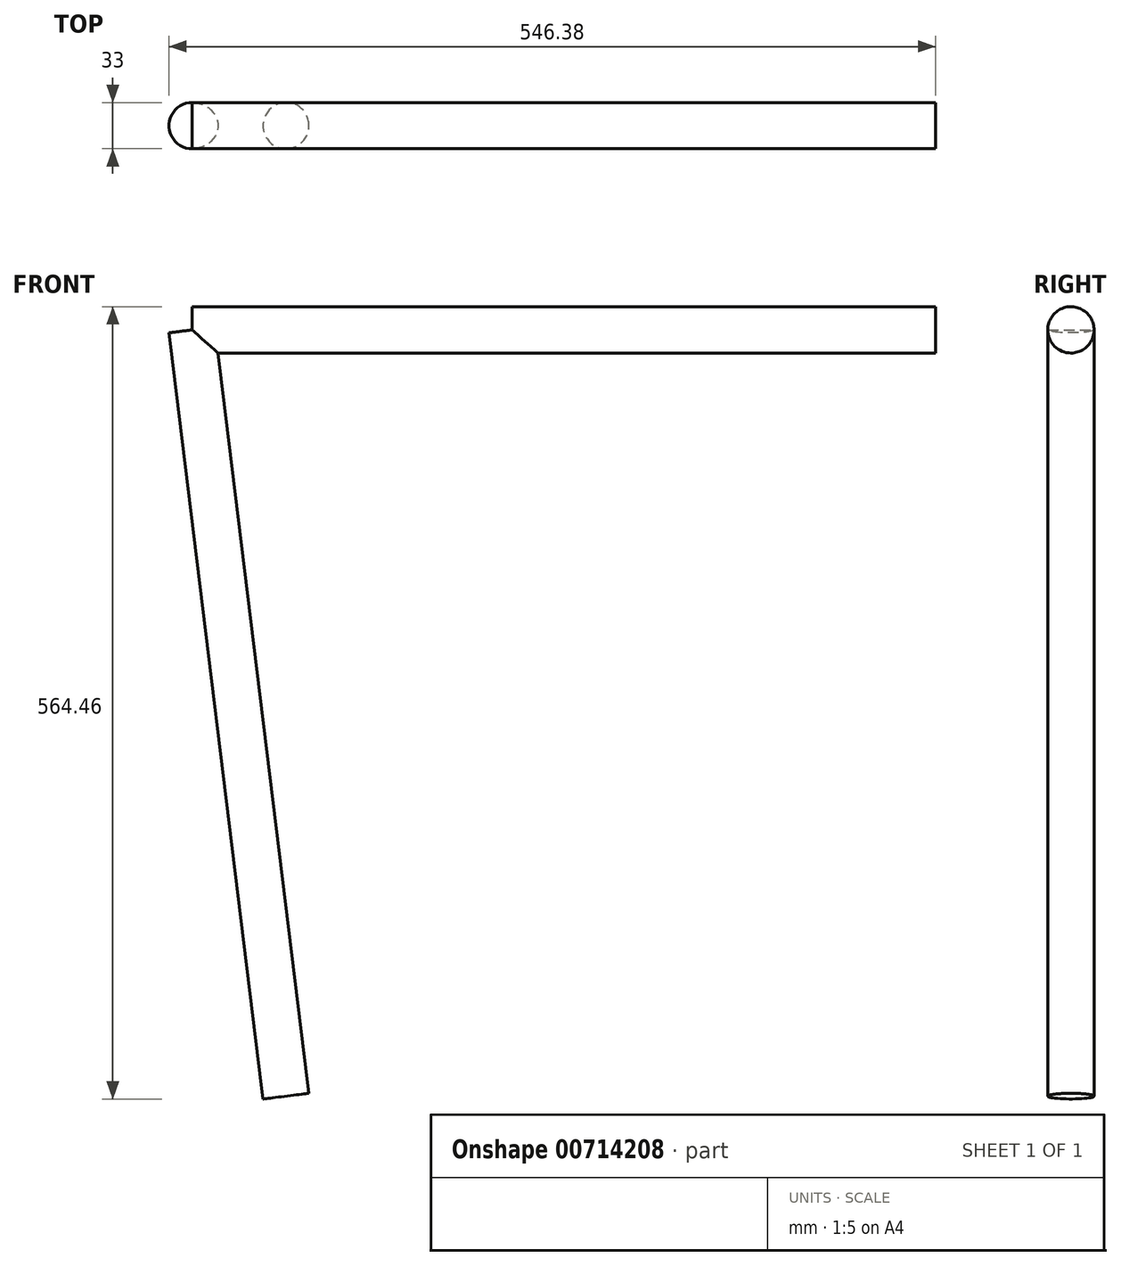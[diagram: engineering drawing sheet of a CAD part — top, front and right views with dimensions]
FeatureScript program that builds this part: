
annotation { "Feature Type Name" : "Feature", "Feature Type Description" : "" }
export const myFeature = defineFeature(function(context is Context, id is Id, definition is map)
    precondition{}
    {
        {
            var Q0;
            Q0=qCreatedBy(makeId("Front.planeOp"),FACE);
            var sketch = newSketch(context, id + "F0", { "sketchPlane" : qUnion([Q0])});
            skCircle(sketch, "E0", {"center": v(0, 0) * mm, "radius": 22.5 * mm});
            skLineSegment(sketch, "E1", {"start": v(0, 22.5) * mm, "end": v(-67.03, 568.4) * mm});
            skLineSegment(sketch, "E2", {"start": v(-22.5, 0) * mm, "end": v(-422.5, 0) * mm});
            skLineSegment(sketch, "E3", {"start": v(-422.5, 0) * mm, "end": v(-28.75, 256.63) * mm});
            skLineSegment(sketch, "E4", {"start": v(-67.03, 568.4) * mm, "end": v(462.97, 568.4) * mm});
            skLineSegment(sketch, "E5", {"start": v(462.97, 568.4) * mm, "end": v(462.97, 418.4) * mm});
            skLineSegment(sketch, "E6", {"start": v(462.97, 418.4) * mm, "end": v(16.62, 15.17) * mm});
            skCircle(sketch, "E7", {"center": v(0, 0) * mm, "radius": 20.71 * mm});
            skSolve(sketch);
        }
        {
            var Q0;
            Q0=sQuery(id+"F0.wireOp",EDGE,"E0");
            var Q1;
            Q1=sQuery(id+"F0.wireOp",EDGE,"E7");
            extrude(context, id + "F1", {"bodyType" : ToolBodyType.SURFACE, "surfaceEntities" : qUnion([Q0, Q1]), "depth" : 25 * mm, "offsetDistance" : 25 * mm, "hasSecondDirection" : true, "secondDirectionOppositeDirection" : true, "secondDirectionDepth" : 25 * mm});
        }
        {
            var Q0;
            Q0=sQuery(id+"F0.wireOp",EDGE,"E1");
            var Q1;
            Q1=sQuery(id+"F0.wireOp",VERTEX,"E1.end");
            cPlane(context, id + "F2", {"entities" : qUnion([Q0, Q1]), "cplaneType" : CPlaneType.LINE_POINT, "offset" : 25 * mm, "width" : 150 * mm, "height" : 150 * mm});
        }
        {
            var Q0;
            Q0=qCreatedBy(id+"F2.planeOp",FACE);
            var sketch = newSketch(context, id + "F3", { "sketchPlane" : qUnion([Q0])});
            skCircle(sketch, "E8", {"center": v(2.74, 0) * mm, "radius": 16.5 * mm});
            skSolve(sketch);
        }
        {
            var Q0;
            Q0=makeQuery(id+"F3.imprint","IMPRINT",FACE,{"disambiguationData":[TD([[makeQuery(id+"F3.imprint","IMPRINT",EDGE,{"derivedFrom":sQuery(id+"F3.wireOp",EDGE,"E8")}),1.0]])]});
            var Q1;
            Q1=sQuery(id+"F0.wireOp",EDGE,"E1");
            sweep(context, id + "F4", {"profiles" : qUnion([Q0]), "surfaceOperationType" : NewSurfaceOperationType.ADD, "path" : qUnion([Q1])});
        }
        {
            var Q0;
            Q0=sQuery(id+"F0.wireOp",EDGE,"E4");
            var Q1;
            Q1=sQuery(id+"F0.wireOp",VERTEX,"E4.end");
            cPlane(context, id + "F5", {"entities" : qUnion([Q0, Q1]), "cplaneType" : CPlaneType.LINE_POINT, "offset" : 25 * mm, "width" : 150 * mm, "height" : 150 * mm});
        }
        {
            var Q0;
            Q0=qCreatedBy(id+"F5.planeOp",FACE);
            var sketch = newSketch(context, id + "F6", { "sketchPlane" : qUnion([Q0])});
            skCircle(sketch, "E9", {"center": v(0, 150.77) * mm, "radius": 16.5 * mm});
            skCircle(sketch, "E10", {"center": v(0, 568.45) * mm, "radius": 16.5 * mm});
            skSolve(sketch);
        }
        {
            var Q0;
            Q0=makeQuery(id+"F6.imprint","IMPRINT",FACE,{"disambiguationData":[TD([[makeQuery(id+"F6.imprint","IMPRINT",EDGE,{"derivedFrom":sQuery(id+"F6.wireOp",EDGE,"E10")}),1.0]])]});
            var Q1;
            Q1=sQuery(id+"F0.wireOp",EDGE,"E4");
            sweep(context, id + "F7", {"operationType" : NewBodyOperationType.ADD, "profiles" : qUnion([Q0]), "path" : qUnion([Q1])});
        }
    });
